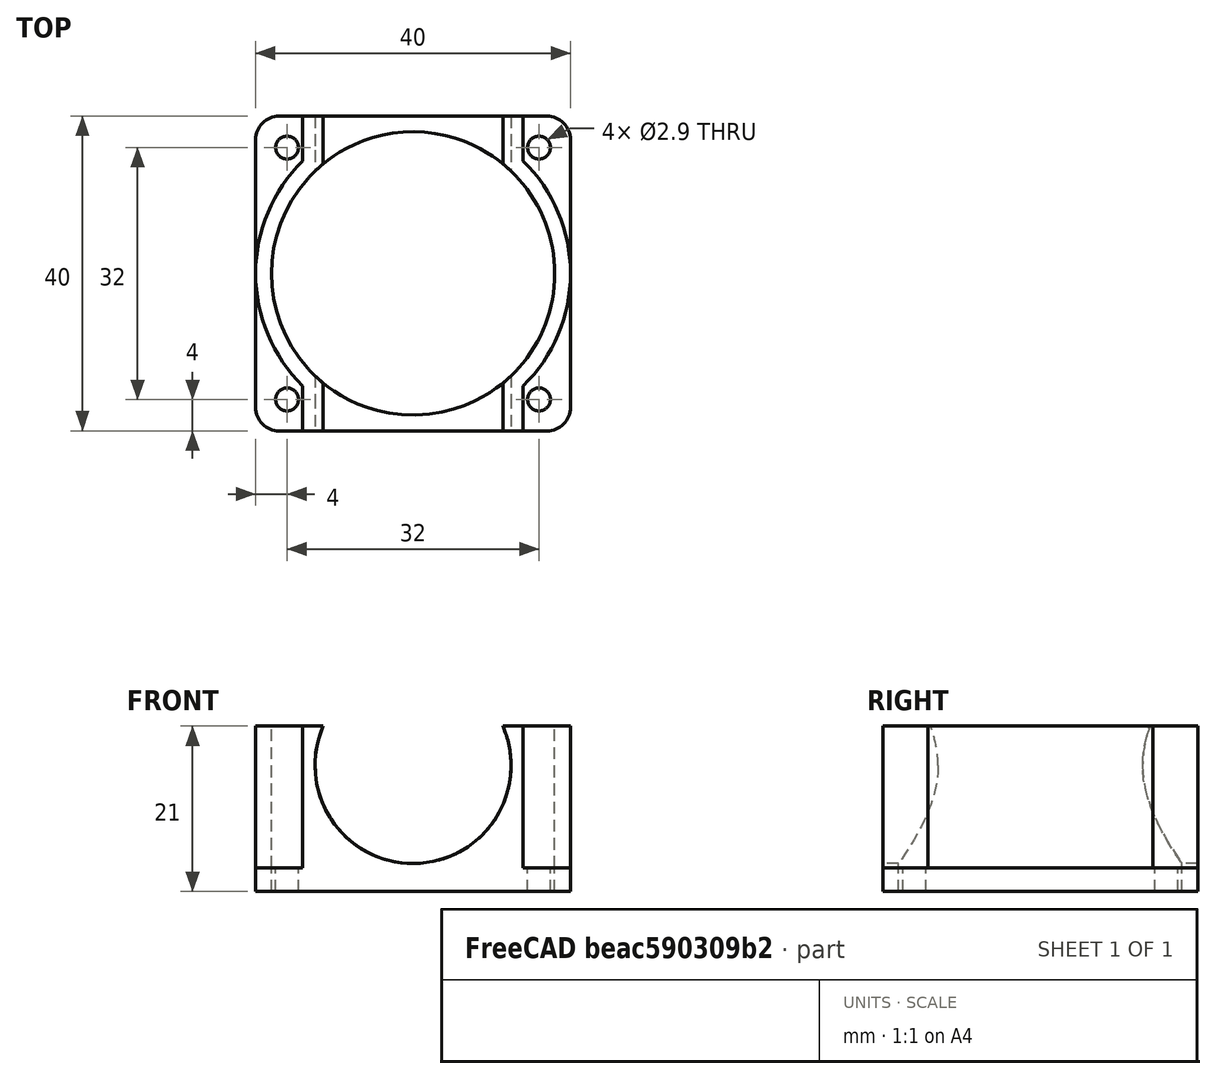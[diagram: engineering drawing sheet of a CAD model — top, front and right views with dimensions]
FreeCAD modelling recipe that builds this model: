
FCSTD DOCUMENT
Label: wentyl v5 fi25
License: CC-BY 3.0
LicenseURL: http://creativecommons.org/licenses/by/3.0/
objects: Part::Cylinder×6, Part::Cut×6, Part::Box×3, Part::MultiFuse×3, Part::FeaturePython×1, Part::Fillet×1
note: 20 computed .brp shape members not serialized (recipe doc carries the construction recipe); baked Part::Feature solids carry a one-line shape summary decoded from their .brp

FEATURE [Part::Box] Box
  Height = 3
  Length = 40
  Width = 40
FEATURE [Part::Cylinder] Cylinder  label="Fan Mouting holes"
  Angle = 360
  Height = 10
  Radius = 1.45
FEATURE [Part::FeaturePython] Array  # Draft array (typed FeaturePython)
  Angle = 360
  ArrayType = 0
  Axis = (0,0,1)
  Base = -> Cylinder
  Center = (0,0,0)
  IntervalX = (32,0,0)
  IntervalY = (0,32,0)
  IntervalZ = (0,0,1)
  NumberPolar = 1
  NumberX = 2
  NumberY = 2
  NumberZ = 1
  Placement = pos=(4,4,0) rot=(0,0,1;0rad)
FEATURE [Part::Cylinder] Cylinder001
  Angle = 360
  Height = 10
  Placement = pos=(20,20,0) rot=(0,0,1;0rad)
  Radius = 18
FEATURE [Part::Cut] Cut
  Base = -> Box
  Tool = -> Array
FEATURE [Part::Cut] Cut001
  Base = -> Cut
  Tool = -> Cylinder001
FEATURE [Part::Fillet] Fillet
  Base = -> Cut001
  Edges = 4 edges r=3: [Edge1,Edge3,Edge6,Edge21]
FEATURE [Part::Cylinder] Cylinder002
  Angle = 360
  Height = 55
  Placement = pos=(20,45,16) rot=(1,0,0;1.5708rad)
  Radius = 12.45
FEATURE [Part::Cylinder] Cylinder003
  Angle = 360
  Height = 21
  Placement = pos=(20,20,0) rot=(0,0,1;0rad)
  Radius = 20
FEATURE [Part::Cylinder] Cylinder004
  Angle = 360
  Height = 21
  Placement = pos=(20,20,0) rot=(0,0,1;0rad)
  Radius = 18
FEATURE [Part::Cut] Cut002
  Base = -> Cylinder003
  Tool = -> Cylinder004
FEATURE [Part::MultiFuse] Fusion
  Shapes = -> [Cut002,Fillet]
FEATURE [Part::Cut] Cut003
  Base = -> Fusion
  Tool = -> Cylinder002
FEATURE [Part::Box] Box001
  Height = 21
  Length = 28
  Placement = pos=(6,0,0) rot=(0,0,1;0rad)
  Width = 8
FEATURE [Part::Box] Box001001
  Height = 21
  Length = 28
  Placement = pos=(6,32,0) rot=(0,0,1;0rad)
  Width = 8
FEATURE [Part::Cylinder] Cylinder005
  Angle = 360
  Height = 39
  Placement = pos=(20,20,-6) rot=(0,0,1;0rad)
  Radius = 18
FEATURE [Part::MultiFuse] Fusion001
  Shapes = -> [Box001001,Box001]
FEATURE [Part::Cut] Cut004
  Base = -> Fusion001
  Tool = -> Cylinder005
FEATURE [Part::Cut] Cut005
  Base = -> Cut004
  Tool = -> Cylinder002
FEATURE [Part::MultiFuse] Fusion002
  Shapes = -> [Cut003,Cut005]
